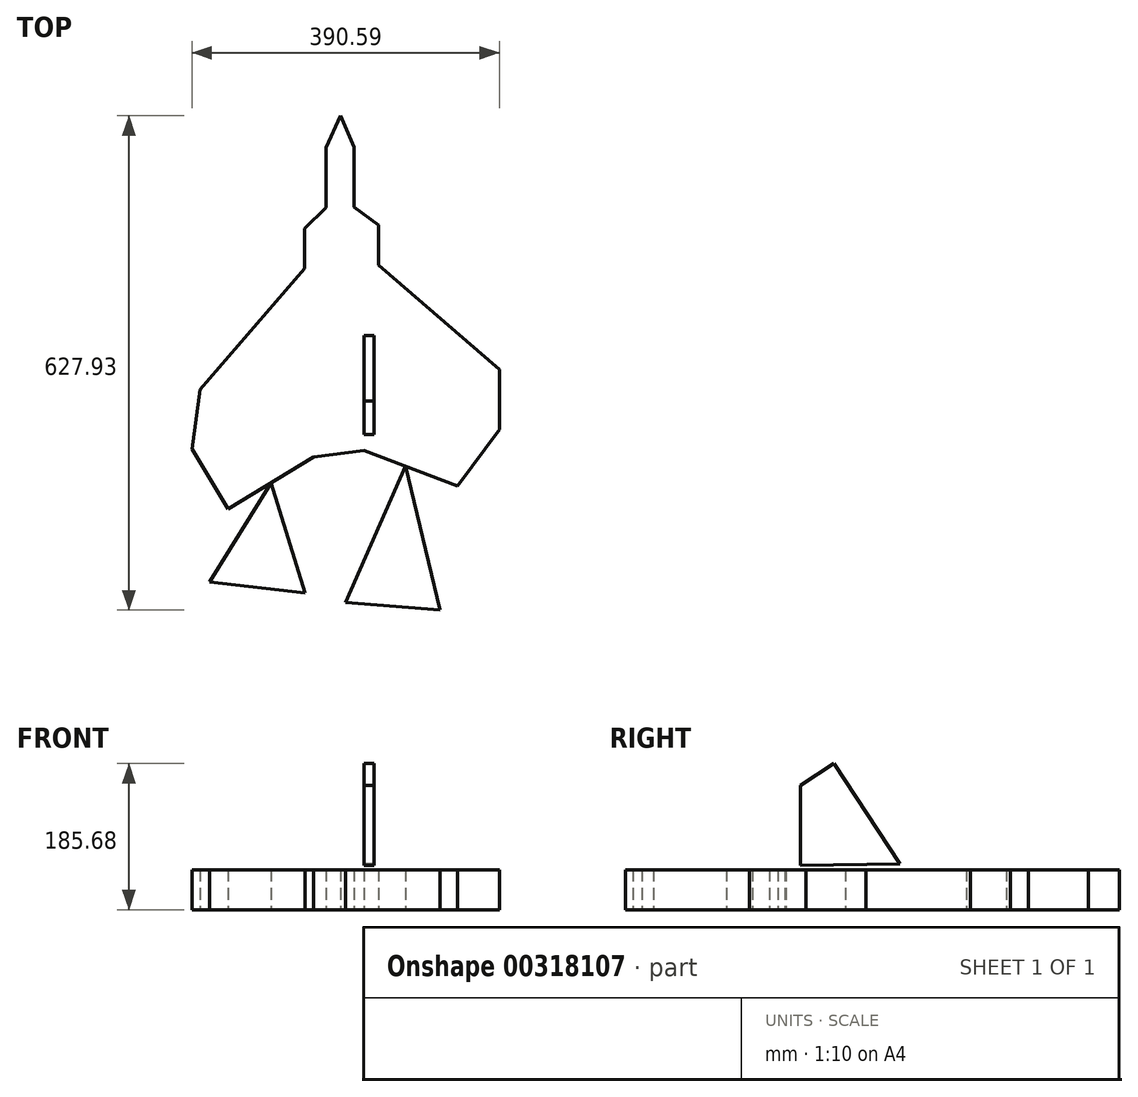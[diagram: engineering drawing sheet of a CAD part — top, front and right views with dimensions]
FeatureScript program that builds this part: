
annotation { "Feature Type Name" : "Feature", "Feature Type Description" : "" }
export const myFeature = defineFeature(function(context is Context, id is Id, definition is map)
    precondition{}
    {
        {
            var Q0;
            Q0=qCreatedBy(makeId("Top.planeOp"),FACE);
            var sketch = newSketch(context, id + "F0", { "sketchPlane" : qUnion([Q0])});
            skLineSegment(sketch, "E0", {"start": v(-48.37, 59.35) * mm, "end": v(-48.37, -16.85) * mm});
            skLineSegment(sketch, "E1", {"start": v(-12.24, 60.08) * mm, "end": v(-12.24, -16.12) * mm});
            skLineSegment(sketch, "E2", {"start": v(-48.37, -16.85) * mm, "end": v(-75.31, -43.8) * mm});
            skLineSegment(sketch, "E3", {"start": v(-12.24, -16.12) * mm, "end": v(18.37, -38.8) * mm});
            skLineSegment(sketch, "E4", {"start": v(-75.31, -43.8) * mm, "end": v(-75.31, -94.6) * mm});
            skLineSegment(sketch, "E5", {"start": v(18.37, -38.8) * mm, "end": v(18.37, -89.6) * mm});
            skLineSegment(sketch, "E6", {"start": v(18.37, -89.6) * mm, "end": v(172, -222.6) * mm});
            skLineSegment(sketch, "E7", {"start": v(-75.31, -94.6) * mm, "end": v(-208.31, -248.22) * mm});
            skLineSegment(sketch, "E8", {"start": v(-208.31, -248.22) * mm, "end": v(-218.59, -323.73) * mm});
            skLineSegment(sketch, "E9", {"start": v(172, -222.6) * mm, "end": v(172, -298.8) * mm});
            skLineSegment(sketch, "E10", {"start": v(-48.37, -16.85) * mm, "end": v(-12.24, -16.12) * mm});
            skLineSegment(sketch, "E11", {"start": v(-218.59, -323.73) * mm, "end": v(-172.5, -399.74) * mm});
            skLineSegment(sketch, "E12", {"start": v(172, -298.8) * mm, "end": v(119.07, -370.22) * mm});
            skLineSegment(sketch, "E13", {"start": v(-172.5, -399.74) * mm, "end": v(-63.9, -333.9) * mm});
            skLineSegment(sketch, "E14", {"start": v(119.07, -370.22) * mm, "end": v(0.35, -325.11) * mm});
            skLineSegment(sketch, "E15", {"start": v(-118.2, -366.82) * mm, "end": v(-196.23, -492.54) * mm});
            skLineSegment(sketch, "E16", {"start": v(53.2, -345.2) * mm, "end": v(96.74, -528.12) * mm});
            skLineSegment(sketch, "E17", {"start": v(96.74, -528.12) * mm, "end": v(-23.51, -518.62) * mm});
            skLineSegment(sketch, "E18", {"start": v(-23.51, -518.62) * mm, "end": v(53.2, -345.2) * mm});
            skLineSegment(sketch, "E19", {"start": v(-196.23, -492.54) * mm, "end": v(-74.7, -506.56) * mm});
            skLineSegment(sketch, "E20", {"start": v(-74.7, -506.56) * mm, "end": v(-118.2, -366.82) * mm});
            skLineSegment(sketch, "E21", {"start": v(0.35, -325.11) * mm, "end": v(-63.9, -333.9) * mm});
            skLineSegment(sketch, "E22", {"start": v(-12.24, 60.08) * mm, "end": v(-29.6, 99.81) * mm});
            skLineSegment(sketch, "E23", {"start": v(-48.37, 59.35) * mm, "end": v(-29.6, 99.81) * mm});
            skSolve(sketch);
        }
        {
            var Q0;
            Q0=makeQuery(id+"F0.imprint","IMPRINT",FACE,{"disambiguationData":[TD([[makeQuery(id+"F0.imprint","IMPRINT",EDGE,{"derivedFrom":sQuery(id+"F0.wireOp",EDGE,"E2")}),1.0]])]});
            var Q1;
            Q1=makeQuery(id+"F0.imprint","IMPRINT",FACE,{"disambiguationData":[TD([[makeQuery(id+"F0.imprint","IMPRINT",EDGE,{"derivedFrom":sQuery(id+"F0.wireOp",EDGE,"E0")}),1.0]])]});
            var Q2;
            Q2=makeQuery(id+"F0.imprint","IMPRINT",FACE,{"disambiguationData":[TD([[makeQuery(id+"F0.imprint","IMPRINT",EDGE,{"derivedFrom":sQuery(id+"F0.wireOp",EDGE,"E16")}),-1.0]])]});
            var Q3;
            Q3=makeQuery(id+"F0.imprint","IMPRINT",FACE,{"disambiguationData":[TD([[makeQuery(id+"F0.imprint","IMPRINT",EDGE,{"derivedFrom":sQuery(id+"F0.wireOp",EDGE,"E15")}),1.0]])]});
            extrude(context, id + "F1", {"entities" : qUnion([Q0, Q1, Q2, Q3]), "depth" : 50.8 * mm});
        }
        {
            var Q0;
            Q0=qCreatedBy(makeId("Right.planeOp"),FACE);
            var sketch = newSketch(context, id + "F2", { "sketchPlane" : qUnion([Q0])});
            skLineSegment(sketch, "E24", {"start": v(-305.35, 56.33) * mm, "end": v(-305.35, 157.93) * mm});
            skLineSegment(sketch, "E25", {"start": v(-305.35, 157.93) * mm, "end": v(-262.8, 185.68) * mm});
            skLineSegment(sketch, "E26", {"start": v(-262.8, 185.68) * mm, "end": v(-179.53, 58.05) * mm});
            skLineSegment(sketch, "E27", {"start": v(-179.53, 58.05) * mm, "end": v(-305.35, 56.33) * mm});
            skSolve(sketch);
        }
        {
            var Q0;
            Q0=makeQuery(id+"F2.imprint","IMPRINT",FACE,{"disambiguationData":[TD([[makeQuery(id+"F2.imprint","IMPRINT",EDGE,{"derivedFrom":sQuery(id+"F2.wireOp",EDGE,"E24")}),-1.0]])]});
            extrude(context, id + "F3", {"entities" : qUnion([Q0]), "depth" : 12.7 * mm});
        }
    });
